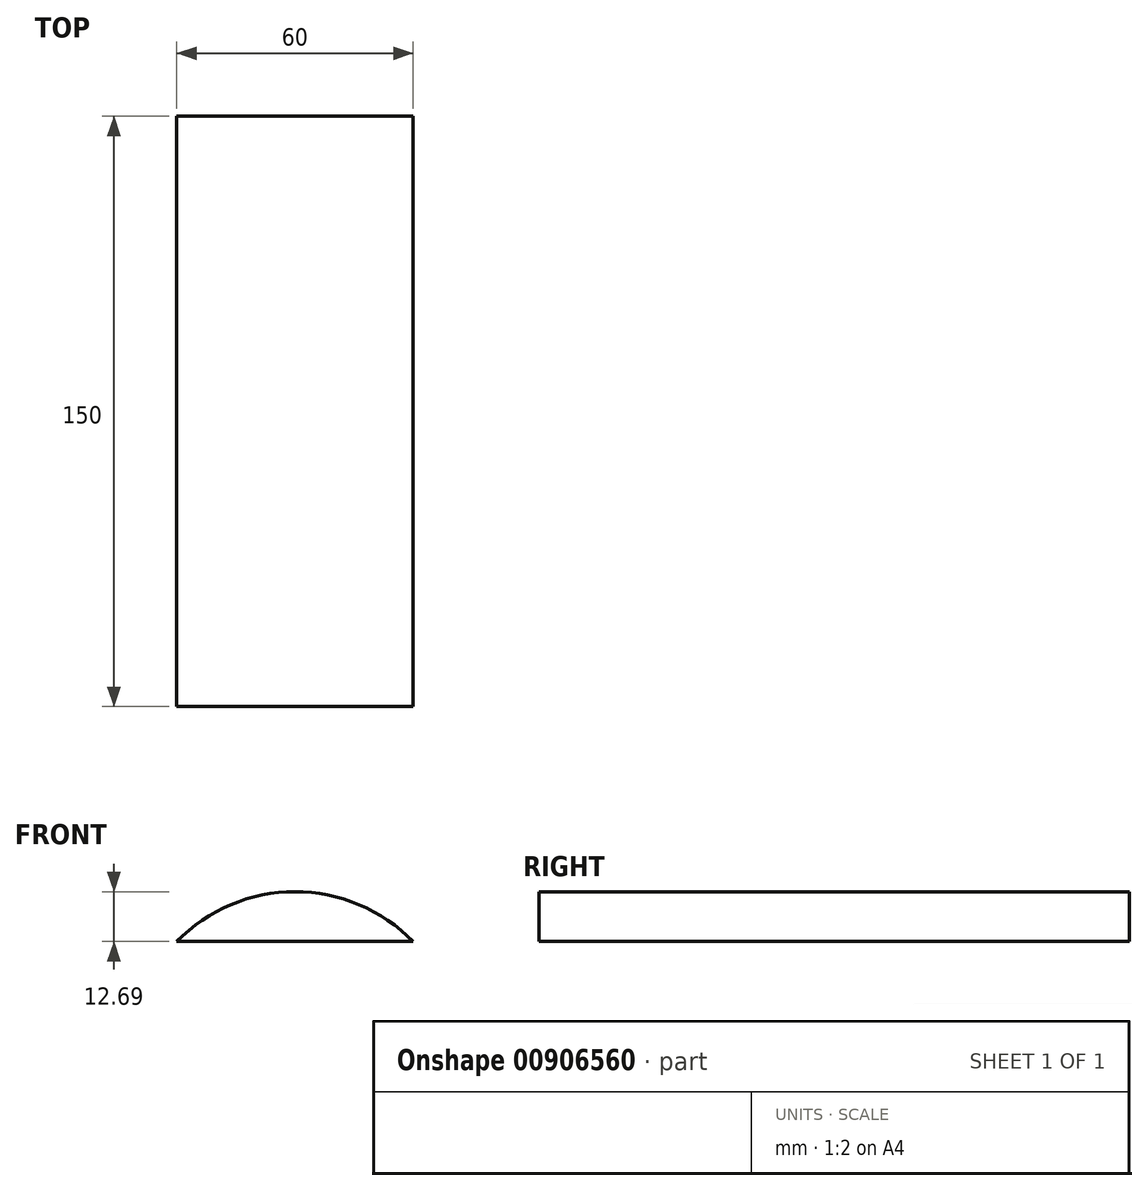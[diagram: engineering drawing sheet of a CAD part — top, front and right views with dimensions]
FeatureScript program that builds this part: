
annotation { "Feature Type Name" : "Feature", "Feature Type Description" : "" }
export const myFeature = defineFeature(function(context is Context, id is Id, definition is map)
    precondition{}
    {
        {
            var Q0;
            Q0=qCreatedBy(makeId("Front.planeOp"),FACE);
            var sketch = newSketch(context, id + "F0", { "sketchPlane" : qUnion([Q0])});
            skLineSegment(sketch, "E0", {"start": v(-45, 0) * mm, "end": v(15, 0) * mm});
            skArc(sketch, "E1", {"start": v(15, 0) * mm, "mid": v(-15, 12.69) * mm, "end": v(-45, 0) * mm});
            skSolve(sketch);
        }
        {
            var Q0;
            Q0=makeQuery(id+"F0.imprint","IMPRINT",FACE,{"disambiguationData":[TD([[makeQuery(id+"F0.imprint","IMPRINT",EDGE,{"derivedFrom":sQuery(id+"F0.wireOp",EDGE,"E0")}),1.0]])]});
            extrude(context, id + "F1", {"entities" : qUnion([Q0]), "oppositeDirection" : true, "depth" : 150 * mm, "offsetDistance" : 25.4 * mm, "symmetric" : true});
        }
    });
